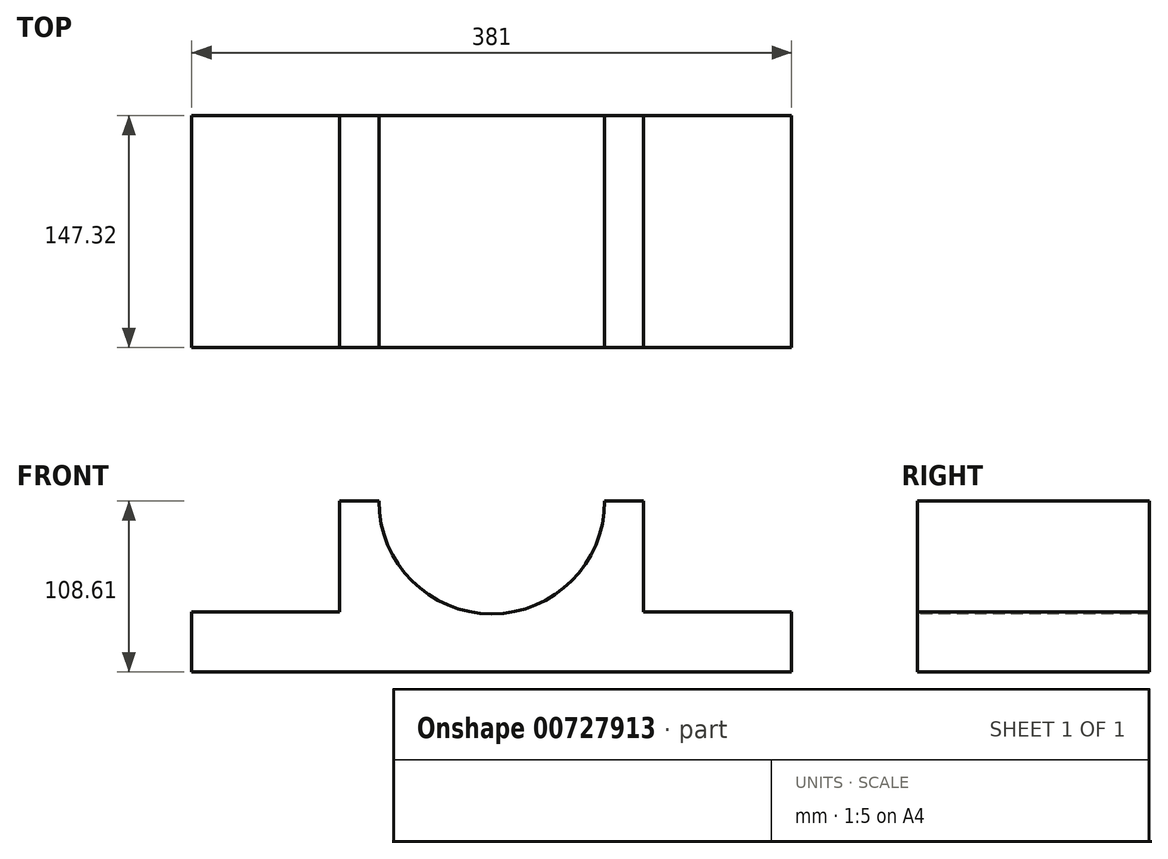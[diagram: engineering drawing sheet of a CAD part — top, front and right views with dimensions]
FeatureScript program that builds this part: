
annotation { "Feature Type Name" : "Feature", "Feature Type Description" : "" }
export const myFeature = defineFeature(function(context is Context, id is Id, definition is map)
    precondition{}
    {
        {
            var Q0;
            Q0=qCreatedBy(makeId("Front.planeOp"),FACE);
            var sketch = newSketch(context, id + "F0", { "sketchPlane" : qUnion([Q0])});
            skLineSegment(sketch, "E0.bottom", {"start": v(190.5, -19.05) * mm, "end": v(-190.5, -19.05) * mm});
            skLineSegment(sketch, "E0.top", {"start": v(190.5, 19.05) * mm, "end": v(-190.5, 19.05) * mm});
            skLineSegment(sketch, "E0.left", {"start": v(190.5, -19.05) * mm, "end": v(190.5, 19.05) * mm});
            skLineSegment(sketch, "E0.right", {"start": v(-190.5, -19.05) * mm, "end": v(-190.5, 19.05) * mm});
            skPoint(sketch, "E0.middle", {"position": v(0, 0) * mm});
            skLineSegment(sketch, "E1", {"start": v(-96.52, 19.05) * mm, "end": v(-96.52, 89.56) * mm});
            skLineSegment(sketch, "E2", {"start": v(-96.52, 89.56) * mm, "end": v(96.52, 89.56) * mm});
            skLineSegment(sketch, "E3", {"start": v(96.52, 89.56) * mm, "end": v(96.52, 19.05) * mm});
            skSolve(sketch);
        }
        {
            var Q0;
            Q0=makeQuery(id+"F0.imprint","IMPRINT",FACE,{"disambiguationData":[TD([[makeQuery(id+"F0.imprint","IMPRINT",EDGE,{"derivedFrom":sQuery(id+"F0.wireOp",EDGE,"E0.bottom")}),-1.0]])]});
            var Q1;
            {var subQ0=sQuery(id+"F0.wireOp",EDGE,"E1");Q1=makeQuery(id+"F0.imprint","IMPRINT",FACE,{"disambiguationData":[TD([[makeQuery(id+"F0.imprint","IMPRINT",EDGE,{"derivedFrom":subQ0}),-1.0]])]});}
            extrude(context, id + "F1", {"entities" : qUnion([Q0, Q1]), "depth" : 147.32 * mm, "offsetDistance" : 25.4 * mm});
        }
        {
            var Q0;
            Q0=makeQuery(id+"F1.opExtrude","CAP_FACE",FACE,{"disambiguationData":[OSD([sQuery(id+"F0.wireOp",EDGE,"E0.bottom"),sQuery(id+"F0.wireOp",EDGE,"E0.top"),sQuery(id+"F0.wireOp",EDGE,"E0.left"),sQuery(id+"F0.wireOp",EDGE,"E0.right"),sQuery(id+"F0.wireOp",EDGE,"E1"),sQuery(id+"F0.wireOp",EDGE,"E2"),sQuery(id+"F0.wireOp",EDGE,"E3")])],"isStart":false});
            var sketch = newSketch(context, id + "F2", { "sketchPlane" : qUnion([Q0])});
            skCircle(sketch, "E4", {"center": v(0, 89.56) * mm, "radius": 71.69 * mm});
            skSolve(sketch);
        }
        {
            var Q0;
            {var subQ0=sQuery(id+"F2.wireOp",EDGE,"E4");var subQ1=makeQuery(id+"F1.opExtrude","CAP_EDGE",EDGE,{"disambiguationData":[OSD([sQuery(id+"F0.wireOp",EDGE,"E2")])],"isStart":false});var subQ2=makeQuery(id+"F2.imprint","INTERSECT",VERTEX,{"disambiguationData":[OD(0.0)],"derivedFrom":[subQ1,subQ0]});Q0=makeQuery(id+"F2.imprint","IMPRINT",FACE,{"disambiguationData":[TD([[makeQuery(id+"F2.imprint","IMPRINT",EDGE,{"disambiguationData":[TD([[subQ2,-1.0]])],"derivedFrom":subQ0}),1.0]])]});}
            extrude(context, id + "F3", {"entities" : qUnion([Q0]), "operationType" : NewBodyOperationType.REMOVE, "oppositeDirection" : true, "depth" : 25.4 * mm, "offsetDistance" : 25.4 * mm});
        }
        {
            var Q0;
            Q0=makeQuery(id+"F3.boolean.opBoolean","COPY",FACE,{"derivedFrom":makeQuery(id+"F3.opExtrude","CAP_FACE",FACE,{"disambiguationData":[OSD([sQuery(id+"F0.wireOp",EDGE,"E2"),sQuery(id+"F2.wireOp",EDGE,"E4")])],"isStart":false})});
            extrude(context, id + "F4", {"entities" : qUnion([Q0]), "operationType" : NewBodyOperationType.REMOVE, "oppositeDirection" : true, "depth" : 147.32 * mm, "offsetDistance" : 25.4 * mm});
        }
    });
